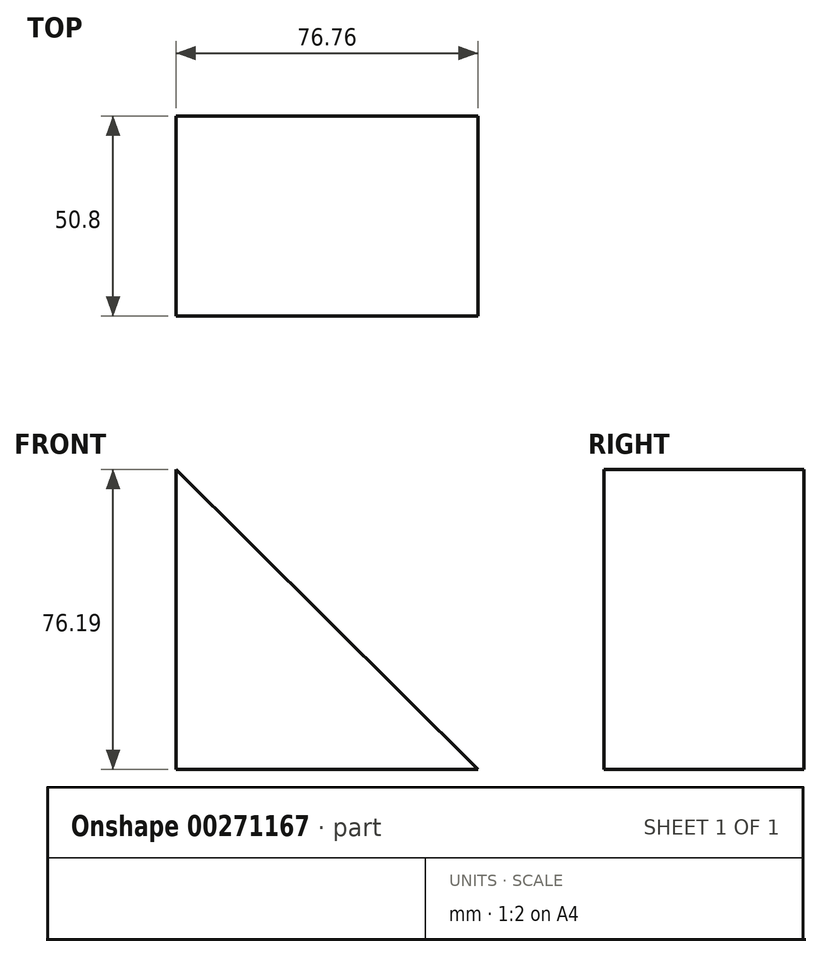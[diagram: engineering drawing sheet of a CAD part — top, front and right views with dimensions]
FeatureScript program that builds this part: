
annotation { "Feature Type Name" : "Feature", "Feature Type Description" : "" }
export const myFeature = defineFeature(function(context is Context, id is Id, definition is map)
    precondition{}
    {
        {
            var Q0;
            Q0=qCreatedBy(makeId("Front.planeOp"),FACE);
            var sketch = newSketch(context, id + "F0", { "sketchPlane" : qUnion([Q0])});
            skLineSegment(sketch, "E0.bottom", {"start": v(-76.76, 76.19) * mm, "end": v(0, 76.19) * mm});
            skLineSegment(sketch, "E0.top", {"start": v(-76.76, 0) * mm, "end": v(0, 0) * mm});
            skLineSegment(sketch, "E0.left", {"start": v(-76.76, 76.19) * mm, "end": v(-76.76, 0) * mm});
            skLineSegment(sketch, "E0.right", {"start": v(0, 76.19) * mm, "end": v(0, 0) * mm});
            skLineSegment(sketch, "E1", {"start": v(-76.76, 76.19) * mm, "end": v(0, 0) * mm});
            skSolve(sketch);
        }
        {
            var Q0;
            Q0=makeQuery(id+"F0.imprint","IMPRINT",FACE,{"disambiguationData":[TD([[makeQuery(id+"F0.imprint","IMPRINT",EDGE,{"derivedFrom":sQuery(id+"F0.wireOp",EDGE,"E0.top")}),1.0]])]});
            extrude(context, id + "F1", {"entities" : qUnion([Q0]), "depth" : 50.8 * mm});
        }
    });
